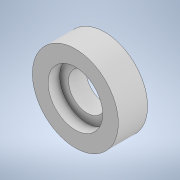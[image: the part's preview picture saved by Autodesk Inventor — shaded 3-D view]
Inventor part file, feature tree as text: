
AUTODESK INVENTOR PART (.ipt)
format: ipt  version: 2021 (Build 250183000, 183)  size: 111,104 bytes
history: native  units: mm
features: extrude x2, sketch x2
ambient origin geometry x8: Origin, YZ Plane, XZ Plane, XY Plane, X Axis, Y Axis, Z Axis, Center Point
bodies: Solid1 (feature_tree)
feature tree (4):
  extrude  "Extrusion1"  Depth=22.0mm
  extrude  "Extrusion2"  Depth=3.0mm
  sketch  "Sketch1"  dims[d0=9.5mm d1=22.0mm]
  sketch  "Sketch2"  dims[d2=7.5mm d3=0.0mm d4=14.0mm d5=3.0mm d6=0.0mm]
